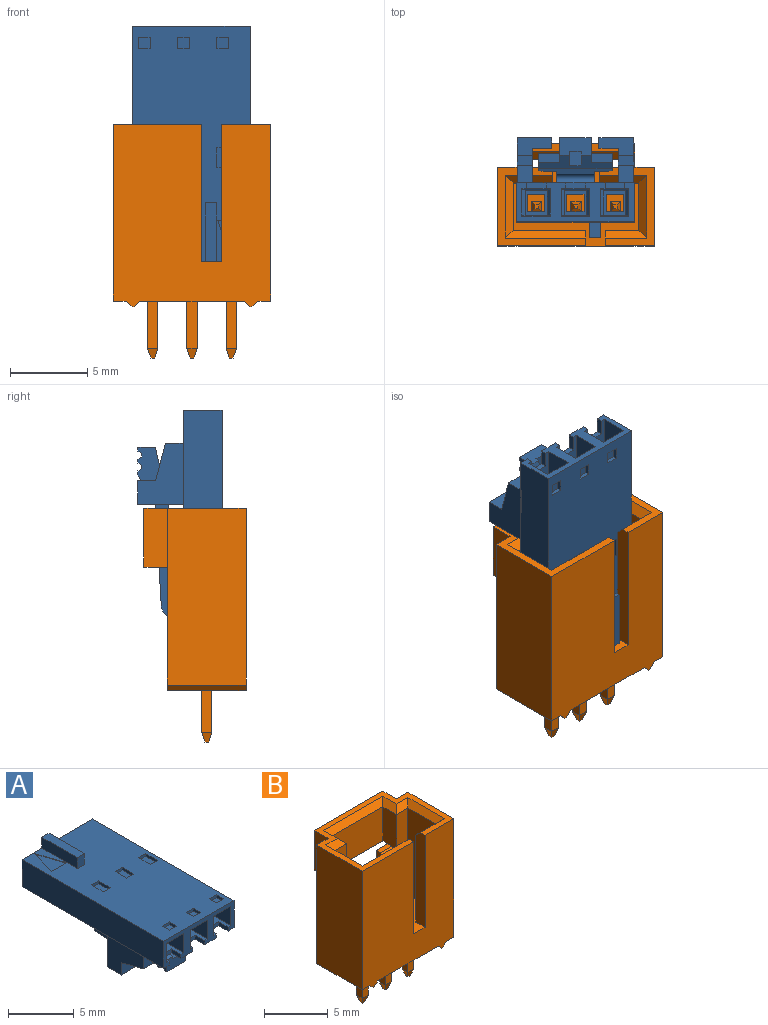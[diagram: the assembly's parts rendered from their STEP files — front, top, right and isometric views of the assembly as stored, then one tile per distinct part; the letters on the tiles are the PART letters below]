
ASSEMBLY  parts=2 mates=1
PART A: 175 faces, bbox 7.6x15.2x6.5 mm
  f0: plane 7.59x2.51mm, normal (0,-1,0), area 7.8mm2, adj f1,f2,f3,f4,f5,f32,f33,f34
  f1: plane 1.02x0.37mm, normal (1,0,0), area 0.4mm2, adj f0,f2,f38,f39
  f2: plane 8.38x1.85mm, normal (0,0,1), area 14.3mm2, adj f0,f1,f3,f5,f7,f39,f40
  f3: plane 8.38x1.78mm, normal (1,0,0), area 14.9mm2, adj f0,f2,f4,f8
  f4: plane 8.38x1.85mm, normal (0,0,-1), area 15.5mm2, adj f0,f3,f5,f9
  f5: plane 8.38x1.78mm, normal (-1,0,0), area 14.9mm2, adj f0,f2,f4,f6
  f6: plane 1.78x0.25mm, normal (-0.76,-0.65,0), area 0.6mm2, adj f5,f7,f9,f11
  f7: plane 1.85x0.25mm, normal (0,-0.29,0.96), area 0.4mm2, adj f2,f6,f8,f12
  f8: plane 1.78x0.25mm, normal (0.76,-0.65,0), area 0.6mm2, adj f3,f7,f9,f13
  f9: plane 1.85x0.25mm, normal (0,-0.29,-0.96), area 0.4mm2, adj f4,f6,f8,f10
  f10: plane 5.79x1.42mm, normal (0,0,-1), area 8.2mm2, adj f9,f11,f13,f14
  f11: plane 5.79x1.63mm, normal (-1,0,0), area 9.4mm2, adj f6,f10,f12,f14
  f12: plane 5.79x1.42mm, normal (0,0,1), area 8.2mm2, adj f7,f11,f13,f14
  f13: plane 5.79x1.63mm, normal (1,0,0), area 9.4mm2, adj f8,f10,f12,f14
  f14: plane 1.63x1.42mm, normal (0,-1,0), area 1.1mm2, adj f10,f11,f12,f13,f15,f16,f17,f18
  f15: plane 1.12x0.46mm, normal (1,0,0), area 0.5mm2, adj f14,f16,f18,f21
  f16: plane 1.12x0.46mm, normal (0,0,-1), area 0.5mm2, adj f14,f15,f17,f22
  f17: plane 1.12x0.46mm, normal (-1,0,0), area 0.5mm2, adj f14,f16,f18,f23
  f18: plane 1.12x0.46mm, normal (0,0,1), area 0.5mm2, adj f14,f15,f17,f19
  f19: plane 1.83x0.36mm, normal (0,0.71,0.71), area 0.7mm2, adj f18,f20,f21,f23
  f20: plane 7.59x3.53mm, normal (0,1,0), area 9.8mm2, adj f19,f21,f22,f23,f24,f25,f26,f27
  f21: plane 1.83x0.36mm, normal (0.71,0.71,0), area 0.7mm2, adj f15,f19,f20,f22
  f22: plane 1.83x0.36mm, normal (0,0.71,-0.71), area 0.7mm2, adj f16,f20,f21,f23
  f23: plane 1.83x0.36mm, normal (-0.71,0.71,0), area 0.7mm2, adj f17,f19,f20,f22
  f24: plane 1.83x0.36mm, normal (0.71,0.71,0), area 0.7mm2, adj f20,f25,f27,f172
  f25: plane 1.83x0.36mm, normal (0,0.71,0.71), area 0.7mm2, adj f20,f24,f26,f173
  f26: plane 1.83x0.36mm, normal (-0.71,0.71,0), area 0.7mm2, adj f20,f25,f27,f174
  f27: plane 1.83x0.36mm, normal (0,0.71,-0.71), area 0.7mm2, adj f20,f24,f26,f28
  f28: plane 1.12x0.46mm, normal (0,0,-1), area 0.5mm2, adj f27,f29,f172,f174
  f29: plane 1.63x1.42mm, normal (0,-1,0), area 1.1mm2, adj f28,f30,f167,f168,f171,f172,f173,f174
  f30: plane 5.79x1.63mm, normal (1,0,0), area 9.4mm2, adj f29,f31,f167,f171
  f31: plane 1.78x0.25mm, normal (0.76,-0.65,0), area 0.6mm2, adj f30,f32,f166,f170
  f32: plane 8.38x1.78mm, normal (1,0,0), area 14.9mm2, adj f0,f31,f33,f35
  f33: plane 8.38x1.85mm, normal (0,0,-1), area 15.5mm2, adj f0,f32,f34,f170
  f34: plane 8.38x1.78mm, normal (-1,0,0), area 14.9mm2, adj f0,f33,f35,f169
  f35: plane 8.38x1.85mm, normal (0,0,1), area 14.3mm2, adj f0,f32,f34,f36,f37,f41,f166
  f36: plane 1.02x0.37mm, normal (1,0,0), area 0.4mm2, adj f0,f35,f37,f38
  f37: plane 1.27x0.37mm, normal (0,-1,0), area 0.5mm2, adj f35,f36,f38,f41
  f38: plane 15.24x7.59mm, normal (0,0,-1), area 100.7mm2, adj f0,f1,f20,f36,f37,f39,f40,f41
  f39: plane 1.27x0.37mm, normal (0,-1,0), area 0.5mm2, adj f1,f2,f38,f40
  f40: plane 1.02x0.37mm, normal (-1,0,0), area 0.4mm2, adj f0,f2,f38,f39
  f41: plane 1.02x0.37mm, normal (-1,0,0), area 0.4mm2, adj f0,f35,f37,f38
  f42: plane 1.02x0.37mm, normal (1,0,0), area 0.4mm2, adj f0,f38,f43,f65
  f43: plane 8.38x1.85mm, normal (0,0,1), area 14.3mm2, adj f0,f42,f44,f46,f48,f64,f65
  f44: plane 8.38x1.78mm, normal (1,0,0), area 14.9mm2, adj f0,f43,f45,f49
  f45: plane 8.38x1.85mm, normal (0,0,-1), area 15.5mm2, adj f0,f44,f46,f50
  f46: plane 8.38x1.78mm, normal (-1,0,0), area 14.9mm2, adj f0,f43,f45,f47
  f47: plane 1.78x0.25mm, normal (-0.76,-0.65,0), area 0.6mm2, adj f46,f48,f50,f52
  f48: plane 1.85x0.25mm, normal (0,-0.29,0.96), area 0.4mm2, adj f43,f47,f49,f53
  f49: plane 1.78x0.25mm, normal (0.76,-0.65,0), area 0.6mm2, adj f44,f48,f50,f54
  f50: plane 1.85x0.25mm, normal (0,-0.29,-0.96), area 0.4mm2, adj f45,f47,f49,f51
  f51: plane 5.79x1.42mm, normal (0,0,-1), area 8.2mm2, adj f50,f52,f54,f55
  f52: plane 5.79x1.63mm, normal (-1,0,0), area 9.4mm2, adj f47,f51,f53,f55
  f53: plane 5.79x1.42mm, normal (0,0,1), area 8.2mm2, adj f48,f52,f54,f55
  f54: plane 5.79x1.63mm, normal (1,0,0), area 9.4mm2, adj f49,f51,f53,f55
  f55: plane 1.63x1.42mm, normal (0,-1,0), area 1.1mm2, adj f51,f52,f53,f54,f56,f57,f58,f59
  f56: plane 1.12x0.46mm, normal (1,0,0), area 0.5mm2, adj f55,f57,f59,f63
  f57: plane 1.12x0.46mm, normal (0,0,-1), area 0.5mm2, adj f55,f56,f58,f62
  f58: plane 1.12x0.46mm, normal (-1,0,0), area 0.5mm2, adj f55,f57,f59,f61
  f59: plane 1.12x0.46mm, normal (0,0,1), area 0.5mm2, adj f55,f56,f58,f60
  f60: plane 1.83x0.36mm, normal (0,0.71,0.71), area 0.7mm2, adj f20,f59,f61,f63
  f61: plane 1.83x0.36mm, normal (-0.71,0.71,0), area 0.7mm2, adj f20,f58,f60,f62
  f62: plane 1.83x0.36mm, normal (0,0.71,-0.71), area 0.7mm2, adj f20,f57,f61,f63
  f63: plane 1.83x0.36mm, normal (0.71,0.71,0), area 0.7mm2, adj f20,f56,f60,f62
  f64: plane 1.02x0.37mm, normal (-1,0,0), area 0.4mm2, adj f0,f38,f43,f65
  f65: plane 1.27x0.37mm, normal (0,-1,0), area 0.5mm2, adj f38,f42,f43,f64
  f66: plane 15.24x2.51mm, normal (1,0,0), area 38.3mm2, adj f0,f20,f38,f67
  f67: plane 15.24x7.59mm, normal (0,0,1), area 106.1mm2, adj f0,f20,f66,f68,f69,f70,f71,f74
  f68: plane 0.76x0.25mm, normal (0,1,0), area 0.2mm2, adj f67,f69,f71,f72
  f69: plane 1.27x0.25mm, normal (1,0,0), area 0.3mm2, adj f67,f68,f70,f72
  f70: plane 0.76x0.25mm, normal (0,-1,0), area 0.2mm2, adj f67,f69,f71,f72
  f71: plane 1.27x0.25mm, normal (-1,0,0), area 0.3mm2, adj f67,f68,f70,f72
  f72: plane 1.27x0.76mm, normal (0,0,1), area 1mm2, adj f68,f69,f70,f71
  f73: plane 0.76x0.76mm, normal (0,0,1), area 0.6mm2, adj f74,f75,f76,f77
  f74: plane 0.76x0.25mm, normal (0,1,0), area 0.2mm2, adj f67,f73,f75,f77
  f75: plane 0.76x0.25mm, normal (1,0,0), area 0.2mm2, adj f67,f73,f74,f76
  f76: plane 0.76x0.25mm, normal (0,-1,0), area 0.2mm2, adj f67,f73,f75,f77
  f77: plane 0.76x0.25mm, normal (-1,0,0), area 0.2mm2, adj f67,f73,f74,f76
  f78: plane 0.76x0.25mm, normal (0,1,0), area 0.2mm2, adj f67,f79,f81,f82
  f79: plane 1.27x0.25mm, normal (1,0,0), area 0.3mm2, adj f67,f78,f80,f82
  f80: plane 0.76x0.25mm, normal (0,-1,0), area 0.2mm2, adj f67,f79,f81,f82
  f81: plane 1.27x0.25mm, normal (-1,0,0), area 0.3mm2, adj f67,f78,f80,f82
  f82: plane 1.27x0.76mm, normal (0,0,1), area 1mm2, adj f78,f79,f80,f81
  f83: plane 0.76x0.76mm, normal (0,0,1), area 0.6mm2, adj f84,f85,f86,f87
  f84: plane 0.76x0.25mm, normal (0,1,0), area 0.2mm2, adj f67,f83,f85,f87
  f85: plane 0.76x0.25mm, normal (1,0,0), area 0.2mm2, adj f67,f83,f84,f86
  f86: plane 0.76x0.25mm, normal (0,-1,0), area 0.2mm2, adj f67,f83,f85,f87
  f87: plane 0.76x0.25mm, normal (-1,0,0), area 0.2mm2, adj f67,f83,f84,f86
  f88: plane 0.76x0.25mm, normal (0,1,0), area 0.2mm2, adj f67,f89,f91,f92
  f89: plane 1.27x0.25mm, normal (1,0,0), area 0.3mm2, adj f67,f88,f90,f92
  f90: plane 0.76x0.25mm, normal (0,-1,0), area 0.2mm2, adj f67,f89,f91,f92
  f91: plane 1.27x0.25mm, normal (-1,0,0), area 0.3mm2, adj f67,f88,f90,f92
  f92: plane 1.27x0.76mm, normal (0,0,1), area 1mm2, adj f88,f89,f90,f91
  f93: plane 0.76x0.76mm, normal (0,0,1), area 0.6mm2, adj f94,f95,f96,f97
  f94: plane 0.76x0.25mm, normal (0,1,0), area 0.2mm2, adj f67,f93,f95,f97
  f95: plane 0.76x0.25mm, normal (1,0,0), area 0.2mm2, adj f67,f93,f94,f96
  f96: plane 0.76x0.25mm, normal (0,-1,0), area 0.2mm2, adj f67,f93,f95,f97
  f97: plane 0.76x0.25mm, normal (-1,0,0), area 0.2mm2, adj f67,f93,f94,f96
  f98: plane 3.81x1.02mm, normal (1,0,0), area 3.9mm2, adj f20,f67,f99,f101
  f99: plane 1.02x0.76mm, normal (0,-1,0), area 0.8mm2, adj f67,f98,f100,f101
  f100: plane 3.81x1.02mm, normal (-1,0,0), area 3.9mm2, adj f20,f67,f99,f101
  f101: plane 3.81x0.76mm, normal (0,0,1), area 2.9mm2, adj f20,f98,f99,f100
  f102: plane 15.24x2.51mm, normal (-1,0,0), area 38.3mm2, adj f0,f20,f38,f67
  f103: plane 2.54x0.81mm, normal (0.95,-0.3,0), area 0.1mm2, adj f67,f104,f105,f106
  f104: plane 2.54x0.81mm, normal (-0.95,-0.3,0), area 0.1mm2, adj f67,f103,f105,f106
  f105: plane 1.63x0.05mm, normal (0,1,0), area 0.1mm2, adj f67,f103,f104,f106
  f106: plane 2.54x1.63mm, normal (0,0,1), area 2.1mm2, adj f103,f104,f105
  f107: plane 3.94x2.24mm, normal (-1,0,0), area 6.9mm2, adj f38,f108,f109,f111,f114,f115
  f108: plane 1.52x1.26mm, normal (0,0,1), area 1.9mm2, adj f107,f109,f111,f112
  f109: plane 2.25x1.14mm, normal (0,-1,0), area 2mm2, adj f107,f108,f110,f112,f113,f114
  f110: plane 2.25x1.52mm, normal (0,0,-1), area 3.4mm2, adj f109,f111,f112,f113
  f111: plane 2.92x2.25mm, normal (0,1,0), area 3.8mm2, adj f38,f107,f108,f110,f112,f113
  f112: plane 1.52x0.69mm, normal (-1,0,0), area 1mm2, adj f108,f109,f110,f111
  f113: plane 3.94x2.92mm, normal (1,0,0), area 8mm2, adj f38,f109,f110,f111,f114,f115
  f114: plane 2.41x0.99mm, normal (0,-0.25,-0.97), area 2.5mm2, adj f107,f109,f113,f115
  f115: plane 1.14x0.99mm, normal (0,-1,0), area 1.1mm2, adj f38,f107,f113,f114
  f116: plane 3.94x2.24mm, normal (1,0,0), area 6.9mm2, adj f38,f117,f118,f120,f123,f124
  f117: plane 1.52x1.26mm, normal (0,0,1), area 1.9mm2, adj f116,f118,f120,f121
  f118: plane 2.92x2.25mm, normal (0,1,0), area 3.8mm2, adj f38,f116,f117,f119,f121,f122
  f119: plane 2.25x1.52mm, normal (0,0,-1), area 3.4mm2, adj f118,f120,f121,f122
  f120: plane 2.25x1.14mm, normal (0,-1,0), area 2mm2, adj f116,f117,f119,f121,f122,f124
  f121: plane 1.52x0.69mm, normal (1,0,0), area 1mm2, adj f117,f118,f119,f120
  f122: plane 3.94x2.92mm, normal (-1,0,0), area 8mm2, adj f38,f118,f119,f120,f123,f124
  f123: plane 1.14x0.99mm, normal (0,-1,0), area 1.1mm2, adj f38,f116,f122,f124
  f124: plane 2.41x0.99mm, normal (0,-0.25,-0.97), area 2.5mm2, adj f116,f120,f122,f123
  f125: plane 4.01x1.6mm, normal (-1,0,0), area 3.9mm2, adj f38,f126,f133,f135,f136,f138,f139
  f126: plane 8.07x4.75mm, normal (0,0.06,-1), area 25.1mm2, adj f125,f127,f128,f129,f130,f132,f133,f134
  f127: plane 2.03x0.64mm, normal (0,-1,0), area 1.3mm2, adj f126,f128,f130,f131
  f128: plane 1.22x0.71mm, normal (1,0,0), area 0.6mm2, adj f126,f127,f129,f131
  f129: plane 2.03x0.71mm, normal (0,0.73,-0.68), area 2mm2, adj f126,f128,f130,f131
  f130: plane 1.22x0.71mm, normal (-1,0,0), area 0.6mm2, adj f126,f127,f129,f131
  f131: plane 2.03x0.56mm, normal (0,0,-1), area 1.1mm2, adj f127,f128,f129,f130
  f132: plane 0.87x0.51mm, normal (-0.71,0.71,0), area 0.6mm2, adj f126,f133,f135,f165
  f133: plane 0.84x0.65mm, normal (0,1,0), area 0.5mm2, adj f125,f126,f132,f135
  f134: plane 0.84x0.65mm, normal (0,1,0), area 0.5mm2, adj f126,f135,f137,f140
  f135: plane 5.94x4.75mm, normal (0,-0.06,1), area 21.9mm2, adj f125,f132,f133,f134,f136,f137,f140,f141
  f136: cylinder r=0.3mm len=2.44mm, axis (1,0,0), area 2.3mm2, adj f38,f125,f135,f137
  f137: plane 4.01x1.6mm, normal (1,0,0), area 3.9mm2, adj f38,f126,f134,f135,f136,f138,f139
  f138: plane 2.44x0.6mm, normal (0,1,0), area 1.5mm2, adj f38,f125,f137,f139
  f139: cylinder r=0.81mm len=2.44mm, axis (1,0,0), area 3mm2, adj f125,f126,f137,f138
  f140: plane 0.87x0.51mm, normal (0.71,0.71,0), area 0.6mm2, adj f126,f134,f135,f141
  f141: plane 4.32x1.09mm, normal (1,0,0), area 3.4mm2, adj f126,f135,f140,f143,f145
  f142: plane 1.36x0.58mm, normal (0,-1,0), area 0.8mm2, adj f126,f144,f145,f165
  f143: plane 1.36x0.58mm, normal (0,-1,0), area 0.8mm2, adj f126,f141,f145,f151
  f144: plane 3.68x1.62mm, normal (-1,0,0), area 4.4mm2, adj f126,f142,f145,f146,f152,f153,f154,f155
  f145: plane 4.75x3.68mm, normal (0,-0.22,0.98), area 9.5mm2, adj f135,f141,f142,f143,f144,f146,f147,f149
  f146: plane 2.03x1.13mm, normal (0,-1,0), area 2.1mm2, adj f144,f145,f147,f148,f149,f151,f164
  f147: plane 3.05x0.93mm, normal (-1,0,0), area 1.8mm2, adj f145,f146,f148,f150
  f148: plane 3.05x0.76mm, normal (0,0,1), area 2.3mm2, adj f146,f147,f149,f150
  f149: plane 3.05x0.93mm, normal (1,0,0), area 1.8mm2, adj f145,f146,f148,f150
  f150: plane 0.93x0.76mm, normal (0,-1,0), area 0.7mm2, adj f145,f147,f148,f149
  f151: plane 3.68x1.62mm, normal (1,0,0), area 4.4mm2, adj f126,f143,f145,f146,f152,f153,f154,f155
  f152: plane 2.03x1.12mm, normal (0,1,0), area 2.3mm2, adj f126,f144,f151,f153
  f153: plane 2.03x1.52mm, normal (0,0,-1), area 3.1mm2, adj f144,f151,f152,f154
  f154: plane 2.03x0.19mm, normal (0,-1,0), area 0.4mm2, adj f144,f151,f153,f155
  f155: plane 2.03x0.38mm, normal (0,0.45,-0.89), area 0.9mm2, adj f144,f151,f154,f156
  f156: plane 2.03x0.25mm, normal (0,0,-1), area 0.5mm2, adj f144,f151,f155,f157
  f157: plane 2.03x0.25mm, normal (0,-0.89,-0.45), area 0.6mm2, adj f144,f151,f156,f158
  f158: plane 2.03x0.25mm, normal (0,0,-1), area 0.5mm2, adj f144,f151,f157,f159
  f159: plane 2.03x0.25mm, normal (0,0.89,-0.45), area 0.6mm2, adj f144,f151,f158,f160
  f160: plane 2.03x0.25mm, normal (0,0,-1), area 0.5mm2, adj f144,f151,f159,f161
  f161: plane 2.03x0.25mm, normal (0,-0.89,-0.45), area 0.6mm2, adj f144,f151,f160,f162
  f162: plane 2.03x0.25mm, normal (0,0,-1), area 0.5mm2, adj f144,f151,f161,f163
  f163: plane 2.03x0.25mm, normal (0,0.89,-0.45), area 0.6mm2, adj f144,f151,f162,f164
  f164: plane 2.03x0.25mm, normal (0,0,-1), area 0.5mm2, adj f144,f146,f151,f163
  f165: plane 4.32x1.09mm, normal (-1,0,0), area 3.4mm2, adj f126,f132,f135,f142,f145
  f166: plane 1.85x0.25mm, normal (0,-0.29,0.96), area 0.4mm2, adj f31,f35,f167,f169
  f167: plane 5.79x1.42mm, normal (0,0,1), area 8.2mm2, adj f29,f30,f166,f168
  f168: plane 5.79x1.63mm, normal (-1,0,0), area 9.4mm2, adj f29,f167,f169,f171
  f169: plane 1.78x0.25mm, normal (-0.76,-0.65,0), area 0.6mm2, adj f34,f166,f168,f170
  f170: plane 1.85x0.25mm, normal (0,-0.29,-0.96), area 0.4mm2, adj f31,f33,f169,f171
  f171: plane 5.79x1.42mm, normal (0,0,-1), area 8.2mm2, adj f29,f30,f168,f170
  f172: plane 1.12x0.46mm, normal (1,0,0), area 0.5mm2, adj f24,f28,f29,f173
  f173: plane 1.12x0.46mm, normal (0,0,1), area 0.5mm2, adj f25,f29,f172,f174
  f174: plane 1.12x0.46mm, normal (-1,0,0), area 0.5mm2, adj f26,f28,f29,f173
PART B: 99 faces, bbox 10.2x6.6x15.1 mm
  f0: plane 11.43x5.08mm, normal (-1,0,0), area 58.1mm2, adj f1,f2,f6,f65
  f1: plane 11.81x10.16mm, normal (0,1,0), area 72mm2, adj f0,f2,f3,f4,f5,f7,f65,f66
  f2: plane 5.08x0.83mm, normal (0,0,-1), area 4.2mm2, adj f0,f1,f5,f6
  f3: plane 6.73x5.08mm, normal (0,0,-1), area 32.9mm2, adj f1,f6,f9,f11,f17,f19,f27,f32
  f4: plane 5.08x0.83mm, normal (0,0,-1), area 4.2mm2, adj f1,f6,f93,f94
  f5: plane 5.08x0.38mm, normal (-0.71,0,-0.71), area 2.7mm2, adj f1,f2,f6,f98
  f6: plane 11.81x10.16mm, normal (0,-1,0), area 105.2mm2, adj f0,f2,f3,f4,f5,f7,f64,f65
  f7: plane 8.13x5.08mm, normal (0,0,1), area 27.9mm2, adj f1,f6,f8,f10,f16,f18,f26,f31
  f8: plane 5.46x0.66mm, normal (-1,0,0), area 3.6mm2, adj f7,f10,f16,f25
  f9: plane 3.05x0.66mm, normal (-1,0,0), area 2mm2, adj f3,f11,f17,f23
  f10: plane 5.46x0.66mm, normal (0,1,0), area 3.6mm2, adj f7,f8,f12,f18
  f11: plane 3.05x0.66mm, normal (0,1,0), area 2mm2, adj f3,f9,f19,f22
  f12: plane 0.66x0.64mm, normal (0,0.95,0.3), area 0.3mm2, adj f10,f13,f14,f25
  f13: plane 0.66x0.64mm, normal (0.95,0,0.3), area 0.3mm2, adj f12,f14,f15,f18
  f14: plane 0.25x0.25mm, normal (0,0,1), area 0.1mm2, adj f12,f13,f15,f25
  f15: plane 0.66x0.64mm, normal (0,-0.95,0.3), area 0.3mm2, adj f13,f14,f16,f25
  f16: plane 5.46x0.66mm, normal (0,-1,0), area 3.6mm2, adj f7,f8,f15,f18
  f17: plane 3.05x0.66mm, normal (0,-1,0), area 2mm2, adj f3,f9,f19,f24
  f18: plane 5.46x0.66mm, normal (1,0,0), area 3.6mm2, adj f7,f10,f13,f16
  f19: plane 3.05x0.66mm, normal (1,0,0), area 2mm2, adj f3,f11,f17,f20
  f20: plane 0.66x0.64mm, normal (0.95,0,-0.3), area 0.3mm2, adj f19,f21,f22,f24
  f21: plane 0.25x0.25mm, normal (0,0,-1), area 0.1mm2, adj f20,f22,f23,f24
  f22: plane 0.66x0.64mm, normal (0,0.95,-0.3), area 0.3mm2, adj f11,f20,f21,f23
  f23: plane 0.66x0.64mm, normal (-0.95,0,-0.3), area 0.3mm2, adj f9,f21,f22,f24
  f24: plane 0.66x0.64mm, normal (0,-0.95,-0.3), area 0.3mm2, adj f17,f20,f21,f23
  f25: plane 0.66x0.64mm, normal (-0.95,0,0.3), area 0.3mm2, adj f8,f12,f14,f15
  f26: plane 5.46x0.66mm, normal (-1,0,0), area 3.6mm2, adj f7,f28,f31,f37
  f27: plane 3.05x0.66mm, normal (-1,0,0), area 2mm2, adj f3,f32,f38,f43
  f28: plane 0.66x0.64mm, normal (-0.95,0,0.3), area 0.3mm2, adj f26,f29,f30,f36
  f29: plane 0.25x0.25mm, normal (0,0,1), area 0.1mm2, adj f28,f30,f35,f36
  f30: plane 0.66x0.64mm, normal (0,0.95,0.3), area 0.3mm2, adj f28,f29,f31,f35
  f31: plane 5.46x0.66mm, normal (0,1,0), area 3.6mm2, adj f7,f26,f30,f33
  f32: plane 3.05x0.66mm, normal (0,1,0), area 2mm2, adj f3,f27,f34,f42
  f33: plane 5.46x0.66mm, normal (1,0,0), area 3.6mm2, adj f7,f31,f35,f37
  f34: plane 3.05x0.66mm, normal (1,0,0), area 2mm2, adj f3,f32,f38,f40
  f35: plane 0.66x0.64mm, normal (0.95,0,0.3), area 0.3mm2, adj f29,f30,f33,f36
  f36: plane 0.66x0.64mm, normal (0,-0.95,0.3), area 0.3mm2, adj f28,f29,f35,f37
  f37: plane 5.46x0.66mm, normal (0,-1,0), area 3.6mm2, adj f7,f26,f33,f36
  f38: plane 3.05x0.66mm, normal (0,-1,0), area 2mm2, adj f3,f27,f34,f39
  f39: plane 0.66x0.64mm, normal (0,-0.95,-0.3), area 0.3mm2, adj f38,f40,f41,f43
  f40: plane 0.66x0.64mm, normal (0.95,0,-0.3), area 0.3mm2, adj f34,f39,f41,f42
  f41: plane 0.25x0.25mm, normal (0,0,-1), area 0.1mm2, adj f39,f40,f42,f43
  f42: plane 0.66x0.64mm, normal (0,0.95,-0.3), area 0.3mm2, adj f32,f40,f41,f43
  f43: plane 0.66x0.64mm, normal (-0.95,0,-0.3), area 0.3mm2, adj f27,f39,f41,f42
  f44: plane 5.46x0.66mm, normal (-1,0,0), area 3.6mm2, adj f7,f46,f49,f55
  f45: plane 3.05x0.66mm, normal (-1,0,0), area 2mm2, adj f3,f50,f56,f61
  f46: plane 0.66x0.64mm, normal (-0.95,0,0.3), area 0.3mm2, adj f44,f47,f48,f54
  f47: plane 0.25x0.25mm, normal (0,0,1), area 0.1mm2, adj f46,f48,f53,f54
  f48: plane 0.66x0.64mm, normal (0,0.95,0.3), area 0.3mm2, adj f46,f47,f49,f53
  f49: plane 5.46x0.66mm, normal (0,1,0), area 3.6mm2, adj f7,f44,f48,f51
  f50: plane 3.05x0.66mm, normal (0,1,0), area 2mm2, adj f3,f45,f52,f60
  f51: plane 5.46x0.66mm, normal (1,0,0), area 3.6mm2, adj f7,f49,f53,f55
  f52: plane 3.05x0.66mm, normal (1,0,0), area 2mm2, adj f3,f50,f56,f58
  f53: plane 0.66x0.64mm, normal (0.95,0,0.3), area 0.3mm2, adj f47,f48,f51,f54
  f54: plane 0.66x0.64mm, normal (0,-0.95,0.3), area 0.3mm2, adj f46,f47,f53,f55
  f55: plane 5.46x0.66mm, normal (0,-1,0), area 3.6mm2, adj f7,f44,f51,f54
  f56: plane 3.05x0.66mm, normal (0,-1,0), area 2mm2, adj f3,f45,f52,f57
  f57: plane 0.66x0.64mm, normal (0,-0.95,-0.3), area 0.3mm2, adj f56,f58,f59,f61
  f58: plane 0.66x0.64mm, normal (0.95,0,-0.3), area 0.3mm2, adj f52,f57,f59,f60
  f59: plane 0.25x0.25mm, normal (0,0,-1), area 0.1mm2, adj f57,f58,f60,f61
  f60: plane 0.66x0.64mm, normal (0,0.95,-0.3), area 0.3mm2, adj f50,f58,f59,f61
  f61: plane 0.66x0.64mm, normal (-0.95,0,-0.3), area 0.3mm2, adj f45,f57,f59,f60
  f62: plane 8.38x4.7mm, normal (0,1,0), area 39.4mm2, adj f7,f64,f76,f78
  f63: plane 8.38x2.16mm, normal (0,1,0), area 18.1mm2, adj f7,f79,f80,f88
  f64: plane 8.89x1.02mm, normal (1,0,0), area 8.9mm2, adj f6,f7,f62,f65,f78
  f65: plane 10.16x6.6mm, normal (0,0,1), area 15.4mm2, adj f0,f1,f6,f64,f66,f69,f70,f77
  f66: plane 3.81x1.52mm, normal (-1,0,0), area 5.8mm2, adj f1,f65,f67,f92
  f67: plane 7.62x1.52mm, normal (0,0,-1), area 8.8mm2, adj f1,f66,f68,f71,f86,f91,f92
  f68: plane 5.59x3.3mm, normal (0,-1,0), area 18.5mm2, adj f67,f69,f71,f86
  f69: plane 6.6x0.51mm, normal (0,-0.71,0.71), area 4.4mm2, adj f65,f68,f70,f87
  f70: plane 2.03x0.51mm, normal (0.71,0,0.71), area 1.1mm2, adj f65,f69,f71,f89
  f71: plane 3.81x1.52mm, normal (1,0,0), area 5.2mm2, adj f67,f68,f70,f72,f75,f90
  f72: plane 1.27x0.51mm, normal (0,0,1), area 0.6mm2, adj f1,f71,f74,f90
  f73: plane 1.27x0.51mm, normal (0,0,1), area 0.6mm2, adj f1,f84,f85,f86
  f74: plane 5.08x1.02mm, normal (1,0,0), area 5mm2, adj f1,f7,f72,f75,f90
  f75: plane 8.38x2.54mm, normal (0,-1,0), area 16.5mm2, adj f7,f71,f74,f76,f89,f90
  f76: plane 8.38x3.05mm, normal (1,0,0), area 25.5mm2, adj f7,f62,f75,f77
  f77: plane 4.06x0.51mm, normal (0.71,0,0.71), area 2.6mm2, adj f65,f76,f78,f89
  f78: plane 5.21x0.51mm, normal (0,0.71,0.71), area 3.6mm2, adj f62,f64,f65,f77
  f79: plane 2.67x0.51mm, normal (0,0.71,0.71), area 1.7mm2, adj f63,f65,f80,f81
  f80: plane 8.89x1.02mm, normal (-1,0,0), area 8.9mm2, adj f6,f7,f63,f65,f79
  f81: plane 4.06x0.51mm, normal (-0.71,0,0.71), area 2.6mm2, adj f65,f79,f82,f88
  f82: plane 1.78x0.51mm, normal (0,-0.71,0.71), area 0.9mm2, adj f65,f81,f83,f87
  f83: plane 8.38x2.54mm, normal (0,-1,0), area 16.5mm2, adj f7,f82,f84,f85,f86,f88
  f84: plane 5.08x1.02mm, normal (-1,0,0), area 5mm2, adj f1,f7,f73,f83,f85
  f85: plane 1.27x0.51mm, normal (0,-0.71,0.71), area 0.9mm2, adj f73,f83,f84,f86
  f86: plane 3.81x1.52mm, normal (-1,0,0), area 5.2mm2, adj f67,f68,f73,f83,f85,f87
  f87: plane 2.03x0.51mm, normal (-0.71,0,0.71), area 1.1mm2, adj f65,f69,f82,f86
  f88: plane 8.38x3.05mm, normal (-1,0,0), area 25.5mm2, adj f7,f63,f81,f83
  f89: plane 1.78x0.51mm, normal (0,-0.71,0.71), area 0.9mm2, adj f65,f70,f75,f77
  f90: plane 1.27x0.51mm, normal (0,-0.71,0.71), area 0.9mm2, adj f71,f72,f74,f75
  f91: plane 3.81x1.52mm, normal (1,0,0), area 5.8mm2, adj f1,f65,f67,f92
  f92: plane 7.62x3.81mm, normal (0,1,0), area 29mm2, adj f65,f66,f67,f91
  f93: plane 11.43x5.08mm, normal (1,0,0), area 58.1mm2, adj f1,f4,f6,f65
  f94: plane 5.08x0.38mm, normal (0.71,0,-0.71), area 2.7mm2, adj f1,f4,f6,f95
  f95: plane 5.08x0.13mm, normal (0,0,-1), area 0.6mm2, adj f1,f6,f94,f96
  f96: plane 5.08x0.38mm, normal (-0.71,0,-0.71), area 2.7mm2, adj f1,f3,f6,f95
  f97: plane 5.08x0.38mm, normal (0.71,0,-0.71), area 2.7mm2, adj f1,f3,f6,f98
  f98: plane 5.08x0.13mm, normal (0,0,-1), area 0.6mm2, adj f1,f5,f6,f97
PLACE A rot(axis=(0,-0.71,0.71),180deg) t=(5.04,2.81,10.16)mm
PLACE B t=(5.08,2.54,7.62)mm
MATE fastened A.f20 <-> B.f7  axis (0,0,-1) through (5.14,2.67,2.54)mm
